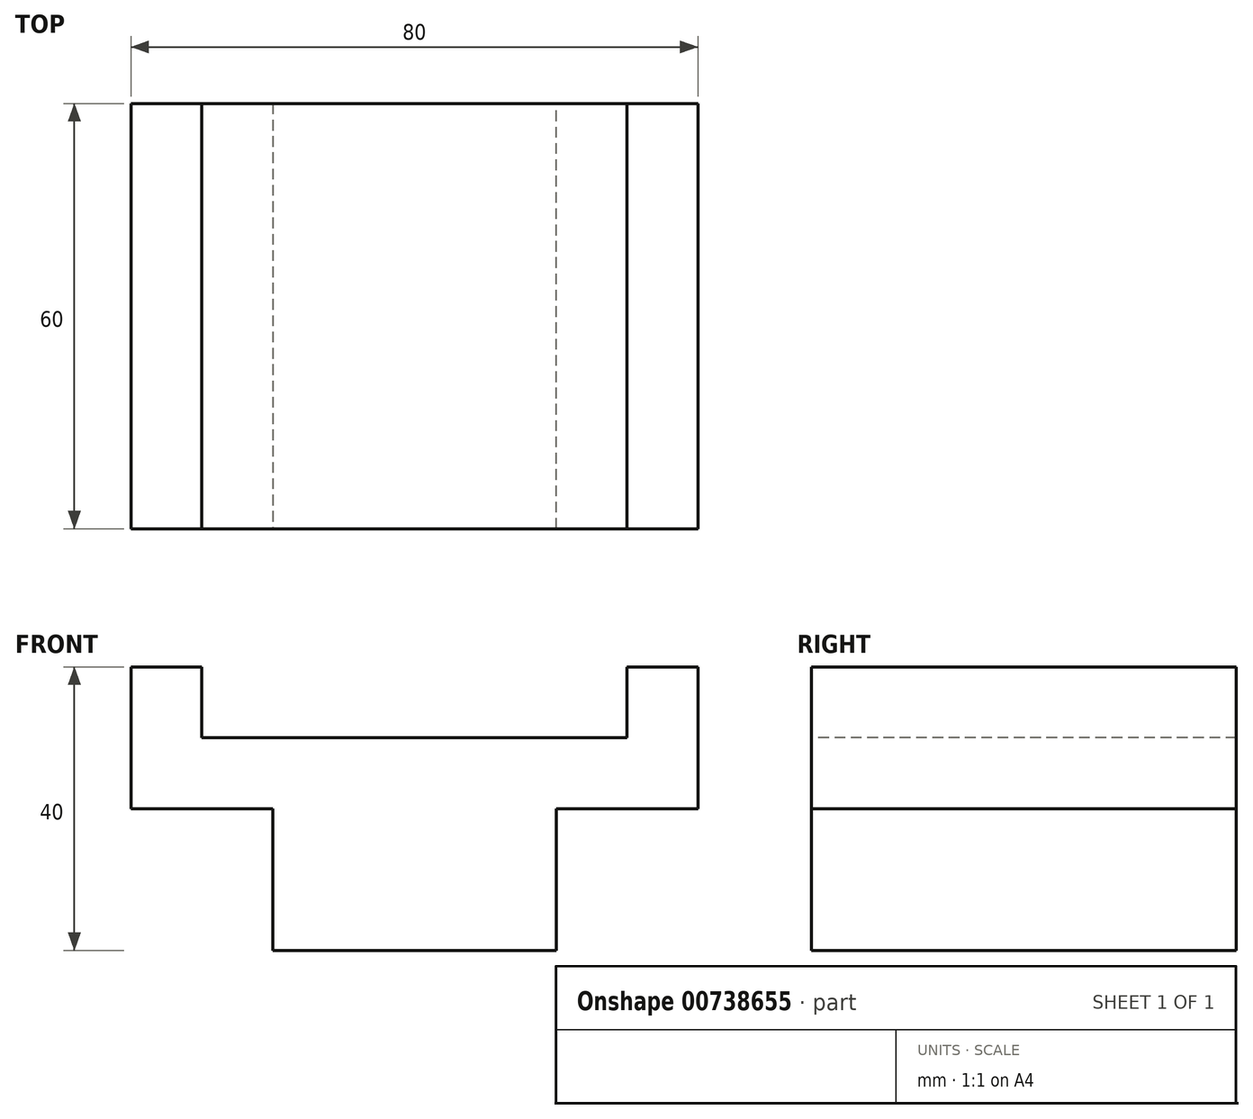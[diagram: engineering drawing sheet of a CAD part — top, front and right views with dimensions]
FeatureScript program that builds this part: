
annotation { "Feature Type Name" : "Feature", "Feature Type Description" : "" }
export const myFeature = defineFeature(function(context is Context, id is Id, definition is map)
    precondition{}
    {
        {
            var Q0;
            Q0=qCreatedBy(makeId("Top.planeOp"),FACE);
            var sketch = newSketch(context, id + "F0", { "sketchPlane" : qUnion([Q0])});
            skLineSegment(sketch, "E0.left", {"start": v(0, 0) * mm, "end": v(0, -60) * mm});
            skLineSegment(sketch, "E0.right", {"start": v(80, 0) * mm, "end": v(80, -60) * mm});
            skLineSegment(sketch, "E1", {"start": v(20, 0) * mm, "end": v(20, -60) * mm});
            skLineSegment(sketch, "E2", {"start": v(60, -60) * mm, "end": v(60, 0) * mm});
            skLineSegment(sketch, "E3", {"start": v(0, 0) * mm, "end": v(20, 0) * mm});
            skLineSegment(sketch, "E4", {"start": v(80, 0) * mm, "end": v(60, 0) * mm});
            skLineSegment(sketch, "E5", {"start": v(60, 0) * mm, "end": v(20, 0) * mm});
            skLineSegment(sketch, "E6", {"start": v(0, -60) * mm, "end": v(20, -60) * mm});
            skLineSegment(sketch, "E7", {"start": v(60, -60) * mm, "end": v(20, -60) * mm});
            skLineSegment(sketch, "E8", {"start": v(60, -60) * mm, "end": v(80, -60) * mm});
            skSolve(sketch);
        }
        {
            var Q0;
            Q0=makeQuery(id+"F0.imprint","IMPRINT",FACE,{"disambiguationData":[TD([[makeQuery(id+"F0.imprint","IMPRINT",EDGE,{"derivedFrom":sQuery(id+"F0.wireOp",EDGE,"E0.left")}),1.0]])]});
            var Q1;
            Q1=makeQuery(id+"F0.imprint","IMPRINT",FACE,{"disambiguationData":[TD([[makeQuery(id+"F0.imprint","IMPRINT",EDGE,{"derivedFrom":sQuery(id+"F0.wireOp",EDGE,"E1")}),1.0]])]});
            var Q2;
            Q2=makeQuery(id+"F0.imprint","IMPRINT",FACE,{"disambiguationData":[TD([[makeQuery(id+"F0.imprint","IMPRINT",EDGE,{"derivedFrom":sQuery(id+"F0.wireOp",EDGE,"E0.right")}),-1.0]])]});
            extrude(context, id + "F1", {"entities" : qUnion([Q0, Q1, Q2]), "depth" : 30 * mm, "offsetDistance" : 25 * mm});
        }
        {
            var Q0;
            Q0=makeQuery(id+"F1.opExtrude","CAP_FACE",FACE,{"disambiguationData":[OSD([sQuery(id+"F0.wireOp",EDGE,"E0.left"),sQuery(id+"F0.wireOp",EDGE,"E0.right"),sQuery(id+"F0.wireOp",EDGE,"E3"),sQuery(id+"F0.wireOp",EDGE,"E4"),sQuery(id+"F0.wireOp",EDGE,"E5"),sQuery(id+"F0.wireOp",EDGE,"E6"),sQuery(id+"F0.wireOp",EDGE,"E7"),sQuery(id+"F0.wireOp",EDGE,"E8")])],"isStart":false});
            var sketch = newSketch(context, id + "F2", { "sketchPlane" : qUnion([Q0])});
            skLineSegment(sketch, "E9", {"start": v(0, 0) * mm, "end": v(10, 0) * mm});
            skLineSegment(sketch, "E10", {"start": v(10, -60) * mm, "end": v(10, 0) * mm});
            skLineSegment(sketch, "E11", {"start": v(10, -60) * mm, "end": v(0, -60) * mm});
            skLineSegment(sketch, "E12", {"start": v(0, -60) * mm, "end": v(0, 0) * mm});
            skLineSegment(sketch, "E13", {"start": v(80, 0) * mm, "end": v(70, 0) * mm});
            skLineSegment(sketch, "E14", {"start": v(70, 0) * mm, "end": v(70, -60) * mm});
            skLineSegment(sketch, "E15", {"start": v(70, -60) * mm, "end": v(80, -60) * mm});
            skLineSegment(sketch, "E16", {"start": v(80, -60) * mm, "end": v(80, 0) * mm});
            skSolve(sketch);
        }
        {
            var Q0;
            Q0 = qSketchRegion(id + "F2", true);
            var Q1;
            Q1=makeQuery(id+"F0.imprint","IMPRINT",FACE,{"disambiguationData":[TD([[makeQuery(id+"F0.imprint","IMPRINT",EDGE,{"derivedFrom":sQuery(id+"F0.wireOp",EDGE,"E0.left")}),1.0]])]});
            var Q2;
            Q2=makeQuery(id+"F0.imprint","IMPRINT",FACE,{"disambiguationData":[TD([[makeQuery(id+"F0.imprint","IMPRINT",EDGE,{"derivedFrom":sQuery(id+"F0.wireOp",EDGE,"E0.right")}),-1.0]])]});
            extrude(context, id + "F3", {"entities" : qUnion([Q0, Q1, Q2]), "operationType" : NewBodyOperationType.REMOVE, "depth" : 20 * mm, "offsetDistance" : 25 * mm});
        }
        {
            var Q0;
            Q0 = qSketchRegion(id + "F2", true);
            extrude(context, id + "F4", {"entities" : qUnion([Q0]), "operationType" : NewBodyOperationType.ADD, "depth" : 10 * mm, "offsetDistance" : 25 * mm});
        }
    });
